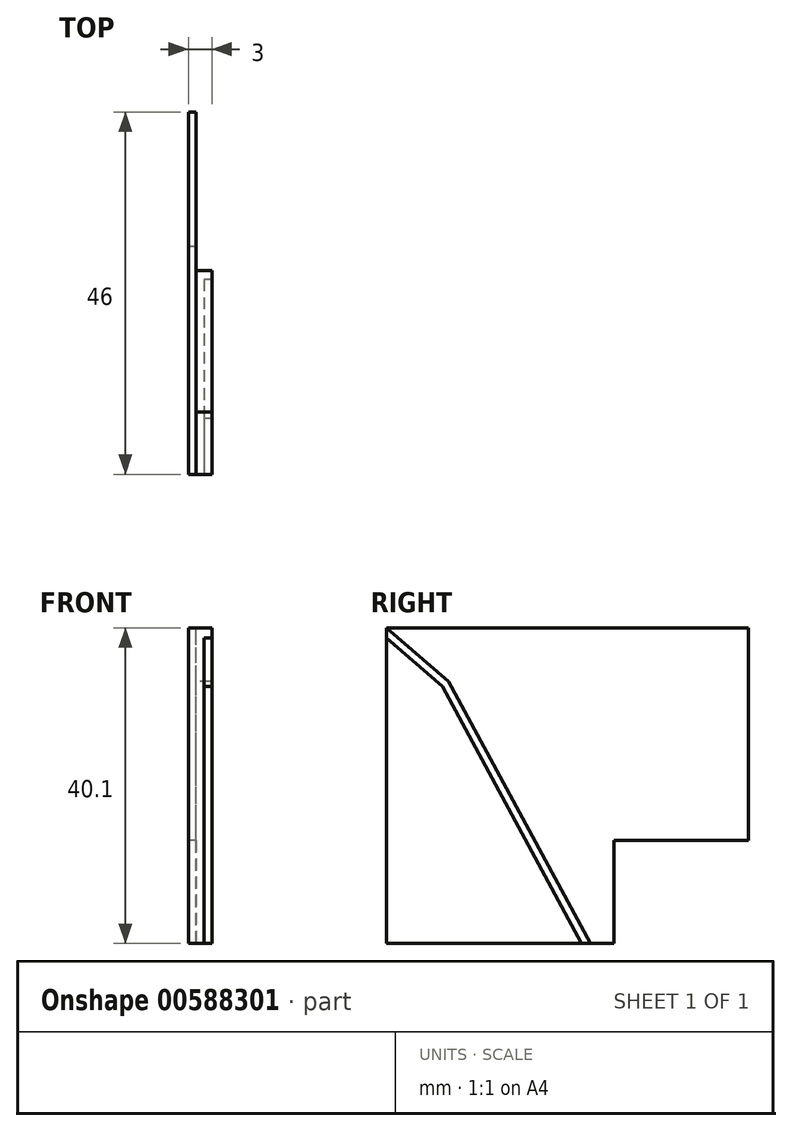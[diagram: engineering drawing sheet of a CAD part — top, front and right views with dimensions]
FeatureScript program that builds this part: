
annotation { "Feature Type Name" : "Feature", "Feature Type Description" : "" }
export const myFeature = defineFeature(function(context is Context, id is Id, definition is map)
    precondition{}
    {
        {
            var Q0;
            Q0=qCreatedBy(makeId("Right.planeOp"),FACE);
            var sketch = newSketch(context, id + "F0", { "sketchPlane" : qUnion([Q0])});
            skLineSegment(sketch, "E0.0", {"start": v(-35.16, 53.23) * mm, "end": v(-81.16, 53.23) * mm});
            skLineSegment(sketch, "E1.0", {"start": v(-35.16, 26.23) * mm, "end": v(-35.16, 53.23) * mm});
            skPoint(sketch, "E2.0", {"position": v(-40.16, 26.23) * mm});
            skLineSegment(sketch, "E3.0", {"start": v(-63.16, 26.23) * mm, "end": v(-62.35, 26.23) * mm});
            skLineSegment(sketch, "E4.0", {"start": v(-52.27, 26.23) * mm, "end": v(-52.27, 13.13) * mm});
            skLineSegment(sketch, "E5.0", {"start": v(-52.27, 13.13) * mm, "end": v(-81.16, 13.13) * mm});
            skLineSegment(sketch, "E6.0", {"start": v(-81.16, 53.23) * mm, "end": v(-81.16, 26.23) * mm});
            skLineSegment(sketch, "E7.0", {"start": v(-81.16, 26.23) * mm, "end": v(-81.16, 13.13) * mm});
            skLineSegment(sketch, "E8.0", {"start": v(-55.27, 13.13) * mm, "end": v(-73.27, 46.43) * mm});
            skLineSegment(sketch, "E9.0", {"start": v(-56.4, 13.13) * mm, "end": v(-74.06, 45.8) * mm});
            skLineSegment(sketch, "E10.0", {"start": v(-73.27, 46.43) * mm, "end": v(-81.16, 53.23) * mm});
            skLineSegment(sketch, "E11.0", {"start": v(-74.06, 45.8) * mm, "end": v(-81.16, 51.91) * mm});
            skLineSegment(sketch, "E12", {"start": v(-45.16, 26.23) * mm, "end": v(-35.16, 26.23) * mm});
            skLineSegment(sketch, "E13.trimOffspring", {"start": v(-52.27, 26.23) * mm, "end": v(-45.16, 26.23) * mm});
            skLineSegment(sketch, "E14.MirrorCS", {"start": v(-137.16, 53.23) * mm, "end": v(-91.16, 53.23) * mm});
            skLineSegment(sketch, "E15.MirrorCS", {"start": v(-91.16, 53.23) * mm, "end": v(-91.16, 26.23) * mm});
            skLineSegment(sketch, "E16.MirrorCS", {"start": v(-91.16, 26.23) * mm, "end": v(-91.16, 13.13) * mm});
            skLineSegment(sketch, "E17.MirrorCS", {"start": v(-120.06, 13.13) * mm, "end": v(-91.16, 13.13) * mm});
            skLineSegment(sketch, "E18.MirrorCS", {"start": v(-120.06, 26.23) * mm, "end": v(-120.06, 13.13) * mm});
            skLineSegment(sketch, "E19.MirrorCS", {"start": v(-120.06, 26.23) * mm, "end": v(-127.16, 26.23) * mm});
            skLineSegment(sketch, "E20.MirrorCS", {"start": v(-127.16, 26.23) * mm, "end": v(-137.16, 26.23) * mm});
            skLineSegment(sketch, "E21.MirrorCS", {"start": v(-137.16, 26.23) * mm, "end": v(-137.16, 53.23) * mm});
            skLineSegment(sketch, "E22.MirrorCS", {"start": v(-98.27, 45.8) * mm, "end": v(-91.16, 51.91) * mm});
            skLineSegment(sketch, "E23.MirrorCS", {"start": v(-99.06, 46.43) * mm, "end": v(-91.16, 53.23) * mm});
            skLineSegment(sketch, "E24.MirrorCS", {"start": v(-117.06, 13.13) * mm, "end": v(-99.06, 46.43) * mm});
            skLineSegment(sketch, "E25.MirrorCS", {"start": v(-115.92, 13.13) * mm, "end": v(-98.27, 45.8) * mm});
            skPoint(sketch, "E26.end.orphan", {"position": v(-86.16, 13.13) * mm});
            skSolve(sketch);
        }
        {
            var Q0;
            Q0=makeQuery(id+"F0.imprint","IMPRINT",FACE,{"disambiguationData":[TD([[makeQuery(id+"F0.imprint","IMPRINT",EDGE,{"derivedFrom":sQuery(id+"F0.wireOp",EDGE,"E0.0")}),1.0]])]});
            extrude(context, id + "F1", {"entities" : qUnion([Q0]), "depth" : 1 * mm, "offsetDistance" : 25 * mm});
        }
        {
            var Q0;
            {var subQ7=sQuery(id+"F0.wireOp",EDGE,"E9.0");Q0=makeQuery(id+"F0.imprint","IMPRINT",FACE,{"disambiguationData":[TD([[makeQuery(id+"F0.imprint","IMPRINT",EDGE,{"derivedFrom":subQ7}),-1.0]])]});}
            extrude(context, id + "F2", {"entities" : qUnion([Q0]), "operationType" : NewBodyOperationType.ADD, "depth" : 3 * mm, "offsetDistance" : 25 * mm});
        }
        {
            var Q0;
            {var subQ1=sQuery(id+"F0.wireOp",EDGE,"E7.0");Q0=makeQuery(id+"F0.imprint","IMPRINT",FACE,{"disambiguationData":[TD([[makeQuery(id+"F0.imprint","IMPRINT",EDGE,{"derivedFrom":subQ1}),1.0]])]});}
            extrude(context, id + "F3", {"entities" : qUnion([Q0]), "operationType" : NewBodyOperationType.ADD, "depth" : 2 * mm, "offsetDistance" : 25 * mm});
        }
    });
